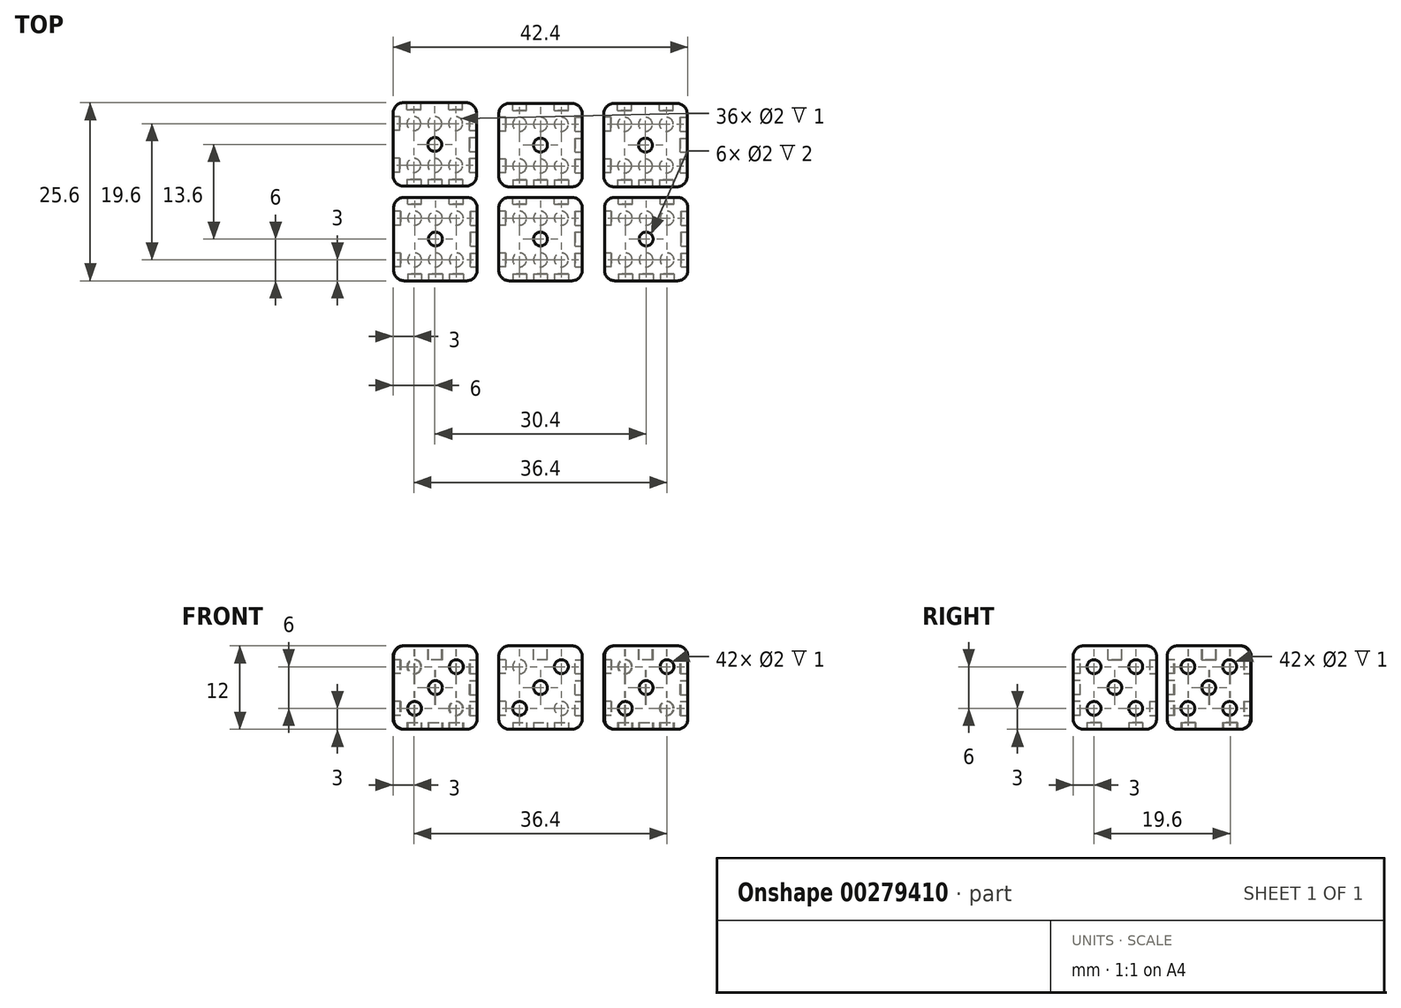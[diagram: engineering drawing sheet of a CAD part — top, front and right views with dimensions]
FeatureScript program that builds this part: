
annotation { "Feature Type Name" : "Feature", "Feature Type Description" : "" }
export const myFeature = defineFeature(function(context is Context, id is Id, definition is map)
    precondition{}
    {
        {
            var Q0;
            Q0=qCreatedBy(makeId("Top.planeOp"),FACE);
            var sketch = newSketch(context, id + "F0", { "sketchPlane" : qUnion([Q0])});
            skLineSegment(sketch, "E0.bottom", {"start": v(-6, 6) * mm, "end": v(6, 6) * mm});
            skLineSegment(sketch, "E0.top", {"start": v(-6, -6) * mm, "end": v(6, -6) * mm});
            skLineSegment(sketch, "E0.left", {"start": v(-6, 6) * mm, "end": v(-6, -6) * mm});
            skLineSegment(sketch, "E0.right", {"start": v(6, 6) * mm, "end": v(6, -6) * mm});
            skPoint(sketch, "E0.middle", {"position": v(0, 0) * mm});
            skSolve(sketch);
        }
        {
            var Q0;
            Q0 = qSketchRegion(id + "F0", true);
            extrude(context, id + "F1", {"entities" : qUnion([Q0]), "depth" : 12 * mm});
        }
        {
            var Q0;
            Q0=makeQuery(id+"F1.opExtrude","CAP_FACE",FACE,{"disambiguationData":[OSD([sQuery(id+"F0.wireOp",EDGE,"E0.bottom"),sQuery(id+"F0.wireOp",EDGE,"E0.top"),sQuery(id+"F0.wireOp",EDGE,"E0.left"),sQuery(id+"F0.wireOp",EDGE,"E0.right")])],"isStart":false});
            var sketch = newSketch(context, id + "F2", { "sketchPlane" : qUnion([Q0])});
            skLineSegment(sketch, "E1", {"start": v(-6, 6) * mm, "end": v(6, -6) * mm, "construction": true});
            skLineSegment(sketch, "E2", {"start": v(6, 6) * mm, "end": v(-6, -6) * mm, "construction": true});
            skLineSegment(sketch, "E3", {"start": v(-6, 0) * mm, "end": v(0, 6) * mm, "construction": true});
            skLineSegment(sketch, "E4", {"start": v(0, 6) * mm, "end": v(6, 0) * mm, "construction": true});
            skLineSegment(sketch, "E5", {"start": v(6, 0) * mm, "end": v(0, -6) * mm, "construction": true});
            skLineSegment(sketch, "E6", {"start": v(0, -6) * mm, "end": v(-6, 0) * mm, "construction": true});
            skCircle(sketch, "E7", {"center": v(0, 0) * mm, "radius": 1 * mm});
            skSolve(sketch);
        }
        {
            var Q0;
            Q0=makeQuery(id+"F2.imprint","IMPRINT",FACE,{"disambiguationData":[TD([[makeQuery(id+"F2.imprint","IMPRINT",EDGE,{"derivedFrom":sQuery(id+"F2.wireOp",EDGE,"E7")}),1.0]])]});
            extrude(context, id + "F3", {"entities" : qUnion([Q0]), "operationType" : NewBodyOperationType.REMOVE, "oppositeDirection" : true, "depth" : 2 * mm});
        }
        {
            var Q0;
            Q0=makeQuery(id+"F1.opExtrude","SWEPT_FACE",FACE,{"disambiguationData":[OSD([sQuery(id+"F0.wireOp",EDGE,"E0.left")])]});
            var sketch = newSketch(context, id + "F4", { "sketchPlane" : qUnion([Q0])});
            skLineSegment(sketch, "E8", {"start": v(-6, 12) * mm, "end": v(6, 0) * mm, "construction": true});
            skLineSegment(sketch, "E9", {"start": v(6, 12) * mm, "end": v(-6, 0) * mm, "construction": true});
            skLineSegment(sketch, "E10", {"start": v(0, 0) * mm, "end": v(-6, 6) * mm, "construction": true});
            skLineSegment(sketch, "E11", {"start": v(-6, 6) * mm, "end": v(0, 12) * mm, "construction": true});
            skLineSegment(sketch, "E12", {"start": v(0, 12) * mm, "end": v(6, 6) * mm, "construction": true});
            skLineSegment(sketch, "E13", {"start": v(6, 6) * mm, "end": v(0, 0) * mm, "construction": true});
            skCircle(sketch, "E14", {"center": v(3, 3) * mm, "radius": 1 * mm});
            skCircle(sketch, "E15", {"center": v(-3, 9) * mm, "radius": 1 * mm});
            skSolve(sketch);
        }
        {
            var Q0;
            Q0=makeQuery(id+"F4.imprint","IMPRINT",FACE,{"disambiguationData":[TD([[makeQuery(id+"F4.imprint","IMPRINT",EDGE,{"derivedFrom":sQuery(id+"F4.wireOp",EDGE,"E15")}),1.0]])]});
            var Q1;
            Q1=makeQuery(id+"F4.imprint","IMPRINT",FACE,{"disambiguationData":[TD([[makeQuery(id+"F4.imprint","IMPRINT",EDGE,{"derivedFrom":sQuery(id+"F4.wireOp",EDGE,"E14")}),1.0]])]});
            extrude(context, id + "F5", {"entities" : qUnion([Q0, Q1]), "operationType" : NewBodyOperationType.REMOVE, "oppositeDirection" : true, "depth" : 1 * mm});
        }
        {
            var Q0;
            Q0=makeQuery(id+"F1.opExtrude","SWEPT_FACE",FACE,{"disambiguationData":[OSD([sQuery(id+"F0.wireOp",EDGE,"E0.top")])]});
            var sketch = newSketch(context, id + "F6", { "sketchPlane" : qUnion([Q0])});
            skLineSegment(sketch, "E16", {"start": v(-6, 12) * mm, "end": v(6, 0) * mm, "construction": true});
            skLineSegment(sketch, "E17", {"start": v(6, 12) * mm, "end": v(-6, 0) * mm, "construction": true});
            skLineSegment(sketch, "E18", {"start": v(0, 0) * mm, "end": v(-6, 6) * mm, "construction": true});
            skLineSegment(sketch, "E19", {"start": v(-6, 6) * mm, "end": v(0, 12) * mm, "construction": true});
            skLineSegment(sketch, "E20", {"start": v(0, 12) * mm, "end": v(6, 6) * mm, "construction": true});
            skLineSegment(sketch, "E21", {"start": v(6, 6) * mm, "end": v(0, 0) * mm, "construction": true});
            skCircle(sketch, "E22", {"center": v(-3, 3) * mm, "radius": 1 * mm});
            skCircle(sketch, "E23", {"center": v(0, 6) * mm, "radius": 1 * mm});
            skCircle(sketch, "E24", {"center": v(3, 9) * mm, "radius": 1 * mm});
            skSolve(sketch);
        }
        {
            var Q0;
            Q0=makeQuery(id+"F6.imprint","IMPRINT",FACE,{"disambiguationData":[TD([[makeQuery(id+"F6.imprint","IMPRINT",EDGE,{"derivedFrom":sQuery(id+"F6.wireOp",EDGE,"E22")}),1.0]])]});
            var Q1;
            Q1=makeQuery(id+"F6.imprint","IMPRINT",FACE,{"disambiguationData":[TD([[makeQuery(id+"F6.imprint","IMPRINT",EDGE,{"derivedFrom":sQuery(id+"F6.wireOp",EDGE,"E23")}),1.0]])]});
            var Q2;
            Q2=makeQuery(id+"F6.imprint","IMPRINT",FACE,{"disambiguationData":[TD([[makeQuery(id+"F6.imprint","IMPRINT",EDGE,{"derivedFrom":sQuery(id+"F6.wireOp",EDGE,"E24")}),1.0]])]});
            extrude(context, id + "F7", {"entities" : qUnion([Q0, Q1, Q2]), "operationType" : NewBodyOperationType.REMOVE, "oppositeDirection" : true, "depth" : 1 * mm});
        }
        {
            var Q0;
            Q0=makeQuery(id+"F1.opExtrude","SWEPT_FACE",FACE,{"disambiguationData":[OSD([sQuery(id+"F0.wireOp",EDGE,"E0.right")])]});
            var sketch = newSketch(context, id + "F8", { "sketchPlane" : qUnion([Q0])});
            skLineSegment(sketch, "E25", {"start": v(-6, 12) * mm, "end": v(6, 0) * mm, "construction": true});
            skLineSegment(sketch, "E26", {"start": v(6, 12) * mm, "end": v(-6, 0) * mm, "construction": true});
            skLineSegment(sketch, "E27", {"start": v(0, 0) * mm, "end": v(-6, 6) * mm, "construction": true});
            skLineSegment(sketch, "E28", {"start": v(-6, 6) * mm, "end": v(0, 12) * mm, "construction": true});
            skLineSegment(sketch, "E29", {"start": v(0, 12) * mm, "end": v(6, 6) * mm, "construction": true});
            skLineSegment(sketch, "E30", {"start": v(6, 6) * mm, "end": v(0, 0) * mm, "construction": true});
            skCircle(sketch, "E31", {"center": v(-3, 3) * mm, "radius": 1 * mm});
            skCircle(sketch, "E32", {"center": v(-3, 9) * mm, "radius": 1 * mm});
            skCircle(sketch, "E33", {"center": v(3, 9) * mm, "radius": 1 * mm});
            skCircle(sketch, "E34", {"center": v(3, 3) * mm, "radius": 1 * mm});
            skCircle(sketch, "E35", {"center": v(0, 6) * mm, "radius": 1 * mm});
            skSolve(sketch);
        }
        {
            var Q0;
            Q0=makeQuery(id+"F8.imprint","IMPRINT",FACE,{"disambiguationData":[TD([[makeQuery(id+"F8.imprint","IMPRINT",EDGE,{"derivedFrom":sQuery(id+"F8.wireOp",EDGE,"E32")}),1.0]])]});
            var Q1;
            Q1=makeQuery(id+"F8.imprint","IMPRINT",FACE,{"disambiguationData":[TD([[makeQuery(id+"F8.imprint","IMPRINT",EDGE,{"derivedFrom":sQuery(id+"F8.wireOp",EDGE,"E33")}),1.0]])]});
            var Q2;
            Q2=makeQuery(id+"F8.imprint","IMPRINT",FACE,{"disambiguationData":[TD([[makeQuery(id+"F8.imprint","IMPRINT",EDGE,{"derivedFrom":sQuery(id+"F8.wireOp",EDGE,"E35")}),1.0]])]});
            var Q3;
            Q3=makeQuery(id+"F8.imprint","IMPRINT",FACE,{"disambiguationData":[TD([[makeQuery(id+"F8.imprint","IMPRINT",EDGE,{"derivedFrom":sQuery(id+"F8.wireOp",EDGE,"E34")}),1.0]])]});
            var Q4;
            Q4=makeQuery(id+"F8.imprint","IMPRINT",FACE,{"disambiguationData":[TD([[makeQuery(id+"F8.imprint","IMPRINT",EDGE,{"derivedFrom":sQuery(id+"F8.wireOp",EDGE,"E31")}),1.0]])]});
            extrude(context, id + "F9", {"entities" : qUnion([Q0, Q1, Q2, Q3, Q4]), "operationType" : NewBodyOperationType.REMOVE, "oppositeDirection" : true, "depth" : 1 * mm});
        }
        {
            var Q0;
            Q0=makeQuery(id+"F1.opExtrude","SWEPT_FACE",FACE,{"disambiguationData":[OSD([sQuery(id+"F0.wireOp",EDGE,"E0.bottom")])]});
            var sketch = newSketch(context, id + "F10", { "sketchPlane" : qUnion([Q0])});
            skLineSegment(sketch, "E36", {"start": v(-6, 12) * mm, "end": v(6, 0) * mm, "construction": true});
            skLineSegment(sketch, "E37", {"start": v(6, 12) * mm, "end": v(-6, 0) * mm, "construction": true});
            skLineSegment(sketch, "E38", {"start": v(0, 0) * mm, "end": v(-6, 6) * mm, "construction": true});
            skLineSegment(sketch, "E39", {"start": v(-6, 6) * mm, "end": v(0, 12) * mm, "construction": true});
            skLineSegment(sketch, "E40", {"start": v(0, 12) * mm, "end": v(6, 6) * mm, "construction": true});
            skLineSegment(sketch, "E41", {"start": v(6, 6) * mm, "end": v(0, 0) * mm, "construction": true});
            skCircle(sketch, "E42", {"center": v(-3, 3) * mm, "radius": 1 * mm});
            skCircle(sketch, "E43", {"center": v(-3, 9) * mm, "radius": 1 * mm});
            skCircle(sketch, "E44", {"center": v(3, 9) * mm, "radius": 1 * mm});
            skCircle(sketch, "E45", {"center": v(3, 3) * mm, "radius": 1 * mm});
            skSolve(sketch);
        }
        {
            var Q0;
            Q0=makeQuery(id+"F10.imprint","IMPRINT",FACE,{"disambiguationData":[TD([[makeQuery(id+"F10.imprint","IMPRINT",EDGE,{"derivedFrom":sQuery(id+"F10.wireOp",EDGE,"E43")}),1.0]])]});
            var Q1;
            Q1=makeQuery(id+"F10.imprint","IMPRINT",FACE,{"disambiguationData":[TD([[makeQuery(id+"F10.imprint","IMPRINT",EDGE,{"derivedFrom":sQuery(id+"F10.wireOp",EDGE,"E44")}),1.0]])]});
            var Q2;
            Q2=makeQuery(id+"F10.imprint","IMPRINT",FACE,{"disambiguationData":[TD([[makeQuery(id+"F10.imprint","IMPRINT",EDGE,{"derivedFrom":sQuery(id+"F10.wireOp",EDGE,"E42")}),1.0]])]});
            var Q3;
            Q3=makeQuery(id+"F10.imprint","IMPRINT",FACE,{"disambiguationData":[TD([[makeQuery(id+"F10.imprint","IMPRINT",EDGE,{"derivedFrom":sQuery(id+"F10.wireOp",EDGE,"E45")}),1.0]])]});
            extrude(context, id + "F11", {"entities" : qUnion([Q0, Q1, Q2, Q3]), "operationType" : NewBodyOperationType.REMOVE, "oppositeDirection" : true, "depth" : 1 * mm});
        }
        {
            var Q0;
            Q0=makeQuery(id+"F1.opExtrude","CAP_FACE",FACE,{"disambiguationData":[OSD([sQuery(id+"F0.wireOp",EDGE,"E0.bottom"),sQuery(id+"F0.wireOp",EDGE,"E0.top"),sQuery(id+"F0.wireOp",EDGE,"E0.left"),sQuery(id+"F0.wireOp",EDGE,"E0.right")])],"isStart":true});
            var sketch = newSketch(context, id + "F12", { "sketchPlane" : qUnion([Q0])});
            skLineSegment(sketch, "E46", {"start": v(-6, -6) * mm, "end": v(6, 6) * mm, "construction": true});
            skLineSegment(sketch, "E47", {"start": v(-6, 6) * mm, "end": v(6, -6) * mm, "construction": true});
            skLineSegment(sketch, "E48", {"start": v(6, 0) * mm, "end": v(0, -6) * mm, "construction": true});
            skLineSegment(sketch, "E49", {"start": v(0, -6) * mm, "end": v(-6, 0) * mm, "construction": true});
            skLineSegment(sketch, "E50", {"start": v(-6, 0) * mm, "end": v(0, 6) * mm, "construction": true});
            skLineSegment(sketch, "E51", {"start": v(0, 6) * mm, "end": v(6, 0) * mm, "construction": true});
            skLineSegment(sketch, "E52", {"start": v(-3, -3) * mm, "end": v(3, -3) * mm, "construction": true});
            skLineSegment(sketch, "E53", {"start": v(-3, 3) * mm, "end": v(3, 3) * mm, "construction": true});
            skCircle(sketch, "E54", {"center": v(-3, -3) * mm, "radius": 1 * mm});
            skCircle(sketch, "E55", {"center": v(0, -3) * mm, "radius": 1 * mm});
            skCircle(sketch, "E56", {"center": v(3, -3) * mm, "radius": 1 * mm});
            skCircle(sketch, "E57", {"center": v(-3, 3) * mm, "radius": 1 * mm});
            skCircle(sketch, "E58", {"center": v(0, 3) * mm, "radius": 1 * mm});
            skCircle(sketch, "E59", {"center": v(3, 3) * mm, "radius": 1 * mm});
            skSolve(sketch);
        }
        {
            var Q0;
            Q0=makeQuery(id+"F12.imprint","IMPRINT",FACE,{"disambiguationData":[TD([[makeQuery(id+"F12.imprint","IMPRINT",EDGE,{"derivedFrom":sQuery(id+"F12.wireOp",EDGE,"E54")}),1.0]])]});
            var Q1;
            Q1=makeQuery(id+"F12.imprint","IMPRINT",FACE,{"disambiguationData":[TD([[makeQuery(id+"F12.imprint","IMPRINT",EDGE,{"derivedFrom":sQuery(id+"F12.wireOp",EDGE,"E55")}),1.0]])]});
            var Q2;
            Q2=makeQuery(id+"F12.imprint","IMPRINT",FACE,{"disambiguationData":[TD([[makeQuery(id+"F12.imprint","IMPRINT",EDGE,{"derivedFrom":sQuery(id+"F12.wireOp",EDGE,"E56")}),1.0]])]});
            var Q3;
            Q3=makeQuery(id+"F12.imprint","IMPRINT",FACE,{"disambiguationData":[TD([[makeQuery(id+"F12.imprint","IMPRINT",EDGE,{"derivedFrom":sQuery(id+"F12.wireOp",EDGE,"E59")}),1.0]])]});
            var Q4;
            Q4=makeQuery(id+"F12.imprint","IMPRINT",FACE,{"disambiguationData":[TD([[makeQuery(id+"F12.imprint","IMPRINT",EDGE,{"derivedFrom":sQuery(id+"F12.wireOp",EDGE,"E58")}),1.0]])]});
            var Q5;
            Q5=makeQuery(id+"F12.imprint","IMPRINT",FACE,{"disambiguationData":[TD([[makeQuery(id+"F12.imprint","IMPRINT",EDGE,{"derivedFrom":sQuery(id+"F12.wireOp",EDGE,"E57")}),1.0]])]});
            extrude(context, id + "F13", {"entities" : qUnion([Q0, Q1, Q2, Q3, Q4, Q5]), "operationType" : NewBodyOperationType.REMOVE, "oppositeDirection" : true, "depth" : 1 * mm});
        }
        {
            var Q0;
            Q0=makeQuery(id+"F1.opExtrude","CAP_EDGE",EDGE,{"disambiguationData":[OSD([sQuery(id+"F0.wireOp",EDGE,"E0.left")])],"isStart":false});
            var Q1;
            Q1=makeQuery(id+"F1.opExtrude","CAP_EDGE",EDGE,{"disambiguationData":[OSD([sQuery(id+"F0.wireOp",EDGE,"E0.bottom")])],"isStart":false});
            var Q2;
            Q2=makeQuery(id+"F1.opExtrude","CAP_EDGE",EDGE,{"disambiguationData":[OSD([sQuery(id+"F0.wireOp",EDGE,"E0.right")])],"isStart":false});
            var Q3;
            Q3=makeQuery(id+"F1.opExtrude","CAP_EDGE",EDGE,{"disambiguationData":[OSD([sQuery(id+"F0.wireOp",EDGE,"E0.top")])],"isStart":false});
            var Q4;
            Q4=makeQuery(id+"F1.opExtrude","SWEPT_EDGE",EDGE,{"disambiguationData":[OSD([sQuery(id+"F0.wireOp",EDGE,"E0.top"),sQuery(id+"F0.wireOp",EDGE,"E0.left")])]});
            var Q5;
            Q5=makeQuery(id+"F1.opExtrude","SWEPT_EDGE",EDGE,{"disambiguationData":[OSD([sQuery(id+"F0.wireOp",EDGE,"E0.top"),sQuery(id+"F0.wireOp",EDGE,"E0.right")])]});
            var Q6;
            Q6=makeQuery(id+"F1.opExtrude","CAP_EDGE",EDGE,{"disambiguationData":[OSD([sQuery(id+"F0.wireOp",EDGE,"E0.top")])],"isStart":true});
            var Q7;
            Q7=makeQuery(id+"F1.opExtrude","CAP_EDGE",EDGE,{"disambiguationData":[OSD([sQuery(id+"F0.wireOp",EDGE,"E0.left")])],"isStart":true});
            var Q8;
            Q8=makeQuery(id+"F1.opExtrude","SWEPT_EDGE",EDGE,{"disambiguationData":[OSD([sQuery(id+"F0.wireOp",EDGE,"E0.bottom"),sQuery(id+"F0.wireOp",EDGE,"E0.left")])]});
            var Q9;
            Q9=makeQuery(id+"F1.opExtrude","SWEPT_EDGE",EDGE,{"disambiguationData":[OSD([sQuery(id+"F0.wireOp",EDGE,"E0.bottom"),sQuery(id+"F0.wireOp",EDGE,"E0.right")])]});
            var Q10;
            Q10=makeQuery(id+"F1.opExtrude","CAP_EDGE",EDGE,{"disambiguationData":[OSD([sQuery(id+"F0.wireOp",EDGE,"E0.right")])],"isStart":true});
            var Q11;
            Q11=makeQuery(id+"F1.opExtrude","CAP_EDGE",EDGE,{"disambiguationData":[OSD([sQuery(id+"F0.wireOp",EDGE,"E0.bottom")])],"isStart":true});
            fillet(context, id + "F14", {"entities" : qUnion([Q0, Q1, Q2, Q3, Q4, Q5, Q6, Q7, Q8, Q9, Q10, Q11]), "radius" : 1.5 * mm, "tangentPropagation" : true, "allowEdgeOverflow" : false});
        }
        {
            var Q0;
            Q0=makeQuery(id+"F1.opExtrude","SWEPT_BODY",BODY,{"disambiguationData":[OSD([sQuery(id+"F0.wireOp",EDGE,"E0.bottom"),sQuery(id+"F0.wireOp",EDGE,"E0.top"),sQuery(id+"F0.wireOp",EDGE,"E0.left"),sQuery(id+"F0.wireOp",EDGE,"E0.right")])]});
            transform(context, id + "F15", {"entities" : qUnion([Q0]), "transformType" : TransformType.TRANSLATION_3D, "dx" : 13.8 * mm, "dy" : 0 * mm, "dz" : 0 * mm, "makeCopy" : true});
        }
        {
            var Q0;
            Q0=makeQuery(id+"F1.opExtrude","SWEPT_BODY",BODY,{"disambiguationData":[OSD([sQuery(id+"F0.wireOp",EDGE,"E0.bottom"),sQuery(id+"F0.wireOp",EDGE,"E0.top"),sQuery(id+"F0.wireOp",EDGE,"E0.left"),sQuery(id+"F0.wireOp",EDGE,"E0.right")])]});
            transform(context, id + "F16", {"entities" : qUnion([Q0]), "transformType" : TransformType.TRANSLATION_3D, "dx" : -14 * mm, "dy" : 0 * mm, "dz" : 0 * mm, "makeCopy" : true});
        }
        {
            var Q0;
            Q0=makeQuery(id+"F1.opExtrude","SWEPT_BODY",BODY,{"disambiguationData":[OSD([sQuery(id+"F0.wireOp",EDGE,"E0.bottom"),sQuery(id+"F0.wireOp",EDGE,"E0.top"),sQuery(id+"F0.wireOp",EDGE,"E0.left"),sQuery(id+"F0.wireOp",EDGE,"E0.right")])]});
            transform(context, id + "F17", {"entities" : qUnion([Q0]), "transformType" : TransformType.TRANSLATION_3D, "dx" : 0 * mm, "dy" : 13.5 * mm, "dz" : 0 * mm, "makeCopy" : true});
        }
        {
            var Q0;
            Q0=makeQuery(id+"F15.opPattern","COPY",BODY,{"derivedFrom":makeQuery(id+"F1.opExtrude","SWEPT_BODY",BODY,{"disambiguationData":[OSD([sQuery(id+"F0.wireOp",EDGE,"E0.bottom"),sQuery(id+"F0.wireOp",EDGE,"E0.top"),sQuery(id+"F0.wireOp",EDGE,"E0.left"),sQuery(id+"F0.wireOp",EDGE,"E0.right")])]}),"instanceName":"1"});
            deleteBodies(context, id + "F18", {"entities" : qUnion([Q0])});
        }
        {
            var Q0;
            Q0=makeQuery(id+"F16.opPattern","COPY",BODY,{"derivedFrom":makeQuery(id+"F1.opExtrude","SWEPT_BODY",BODY,{"disambiguationData":[OSD([sQuery(id+"F0.wireOp",EDGE,"E0.bottom"),sQuery(id+"F0.wireOp",EDGE,"E0.top"),sQuery(id+"F0.wireOp",EDGE,"E0.left"),sQuery(id+"F0.wireOp",EDGE,"E0.right")])]}),"instanceName":"1"});
            deleteBodies(context, id + "F19", {"entities" : qUnion([Q0])});
        }
        {
            var Q0;
            Q0=makeQuery(id+"F1.opExtrude","SWEPT_BODY",BODY,{"disambiguationData":[OSD([sQuery(id+"F0.wireOp",EDGE,"E0.bottom"),sQuery(id+"F0.wireOp",EDGE,"E0.top"),sQuery(id+"F0.wireOp",EDGE,"E0.left"),sQuery(id+"F0.wireOp",EDGE,"E0.right")])]});
            transform(context, id + "F20", {"entities" : qUnion([Q0]), "transformType" : TransformType.TRANSLATION_3D, "dx" : 15.2 * mm, "dy" : 0 * mm, "dz" : 0 * mm, "makeCopy" : true});
        }
        {
            var Q0;
            Q0=makeQuery(id+"F1.opExtrude","SWEPT_BODY",BODY,{"disambiguationData":[OSD([sQuery(id+"F0.wireOp",EDGE,"E0.bottom"),sQuery(id+"F0.wireOp",EDGE,"E0.top"),sQuery(id+"F0.wireOp",EDGE,"E0.left"),sQuery(id+"F0.wireOp",EDGE,"E0.right")])]});
            transform(context, id + "F21", {"entities" : qUnion([Q0]), "transformType" : TransformType.TRANSLATION_3D, "dx" : 15.1 * mm, "dy" : 13.5 * mm, "dz" : 0 * mm, "makeCopy" : true});
        }
        {
            var Q0;
            Q0=makeQuery(id+"F1.opExtrude","SWEPT_BODY",BODY,{"disambiguationData":[OSD([sQuery(id+"F0.wireOp",EDGE,"E0.bottom"),sQuery(id+"F0.wireOp",EDGE,"E0.top"),sQuery(id+"F0.wireOp",EDGE,"E0.left"),sQuery(id+"F0.wireOp",EDGE,"E0.right")])]});
            transform(context, id + "F22", {"entities" : qUnion([Q0]), "transformType" : TransformType.TRANSLATION_3D, "dx" : -15.1 * mm, "dy" : 0 * mm, "dz" : 0 * mm, "makeCopy" : true});
        }
        {
            var Q0;
            Q0=makeQuery(id+"F1.opExtrude","SWEPT_BODY",BODY,{"disambiguationData":[OSD([sQuery(id+"F0.wireOp",EDGE,"E0.bottom"),sQuery(id+"F0.wireOp",EDGE,"E0.top"),sQuery(id+"F0.wireOp",EDGE,"E0.left"),sQuery(id+"F0.wireOp",EDGE,"E0.right")])]});
            transform(context, id + "F23", {"entities" : qUnion([Q0]), "transformType" : TransformType.TRANSLATION_3D, "dx" : -15.2 * mm, "dy" : 13.6 * mm, "dz" : 0 * mm, "makeCopy" : true});
        }
    });
